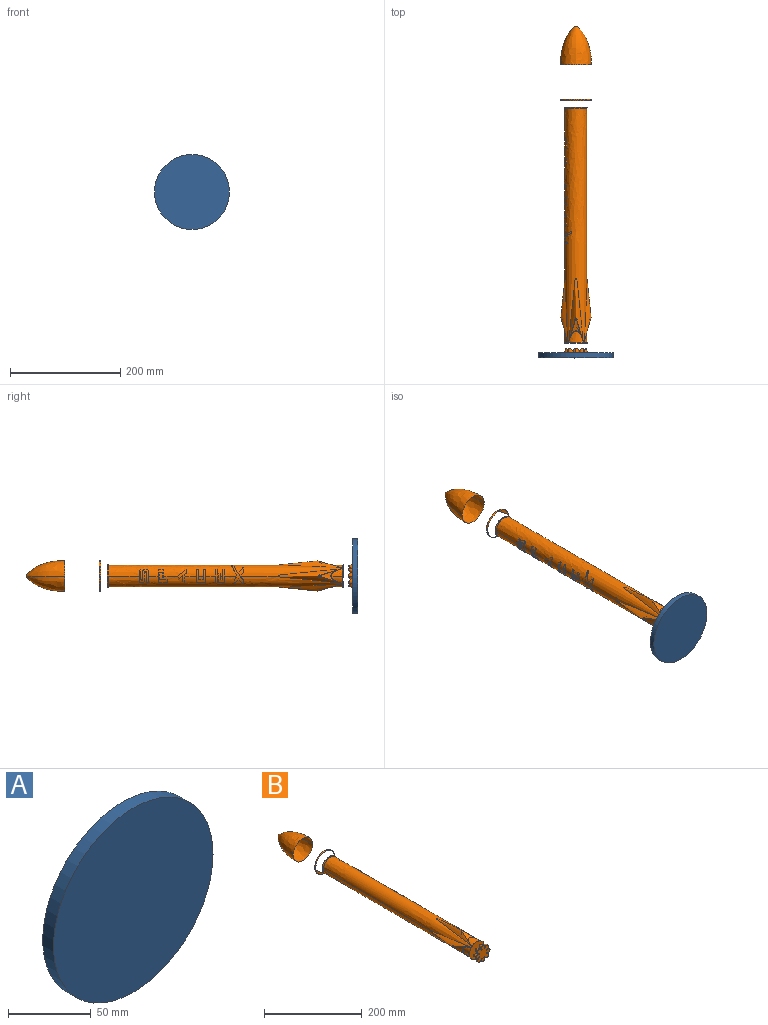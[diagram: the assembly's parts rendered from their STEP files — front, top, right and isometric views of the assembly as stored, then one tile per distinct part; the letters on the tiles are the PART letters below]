
ASSEMBLY  parts=2 mates=1
PART A: 3 faces, bbox 136.1x9.1x136.1 mm
  f0: cylinder r=68.04mm len=136.07mm, axis (0,1,0), area 3890.1mm2, adj f1,f2
  f1: plane 136.07x136.07mm, normal (0,-1,0), area 14542mm2, adj f0
  f2: plane 136.07x136.07mm, normal (0,1,0), area 14542mm2, adj f0
PART B: 144 faces, bbox 56.3x592.9x112.6 mm
  f0: revolved ~5.53x5.53mm, area 27.6mm2, adj f1,f2
  f1: bspline ~69.44x56.06mm, area 4837.5mm2, adj f0,f2,f3
  f2: bspline ~69.44x56.06mm, area 4837.5mm2, adj f0,f1,f3
  f3: revolved ~62.16x56.06mm, area 10948.1mm2, adj f1,f2,f5,f6
  f4: revolved ~13.15x4.18mm, area 53.4mm2, adj f7,f8,f9,f10,f11,f12,f13,f14
  f5: bspline ~56.26x56.26mm, area 228.4mm2, adj f3,f6,f26
  f6: bspline ~56.26x56.26mm, area 228.4mm2, adj f3,f5,f26
  f7: plane 11.52x1.77mm, normal (0,-1,0), area 11.4mm2, adj f4,f8,f14,f32
  f8: bspline ~1.42x1.31mm, area 1.8mm2, adj f4,f7,f9,f32
  f9: plane 1.9x0.94mm, normal (0.33,0,-0.94), area 1.9mm2, adj f4,f8,f10,f32
  f10: bspline ~1.42x1.31mm, area 1.8mm2, adj f4,f9,f11,f32
  f11: plane 11.52x1.77mm, normal (0,1,0), area 11.4mm2, adj f4,f10,f12,f32
  f12: bspline ~1.42x1.31mm, area 1.8mm2, adj f4,f11,f13,f32
  f13: plane 1.9x0.94mm, normal (0.33,0,0.94), area 1.9mm2, adj f4,f12,f14,f32
  f14: bspline ~1.42x1.31mm, area 1.8mm2, adj f4,f7,f13,f32
  f15: revolved ~14.89x8.99mm, area 71.2mm2, adj f42,f43,f44,f45,f46
  f16: bspline ~1.41x1.29mm, area 1.8mm2, adj f17,f36,f50,f51
  f17: plane 2.64x0.95mm, normal (0.31,0,-0.95), area 2.6mm2, adj f16,f18,f36,f51
  f18: bspline ~1.41x1.29mm, area 1.8mm2, adj f17,f36,f51,f52
  f19: bspline ~1.42x1.31mm, area 1.8mm2, adj f20,f34,f57,f58
  f20: plane 7.86x0.94mm, normal (0.34,0,-0.94), area 7.9mm2, adj f19,f21,f34,f58
  f21: bspline ~1.42x1.31mm, area 1.8mm2, adj f20,f34,f58,f59
  f22: bspline ~1.43x1.32mm, area 1.8mm2, adj f23,f31,f70,f71
  f23: plane 0.94x0.91mm, normal (0.35,0,-0.94), area 0.9mm2, adj f22,f24,f31,f71
  f24: bspline ~1.43x1.32mm, area 1.8mm2, adj f23,f31,f71,f72
  f25: plane 0.85x0.53mm, normal (-0.53,0,-0.85), area 0.1mm2, adj f31,f72,f73,f122
  f26: revolved ~54.74x54.74mm, area 2077.2mm2, adj f5,f6,f74,f79
  f27: bspline ~1.44x1.33mm, area 1.8mm2, adj f28,f31,f84,f85
  f28: plane 1.19x0.93mm, normal (0.36,0,0.93), area 1.2mm2, adj f27,f29,f31,f85
  f29: bspline ~1.44x1.33mm, area 1.8mm2, adj f28,f31,f85,f86
  f30: plane 0.81x0.59mm, normal (-0.59,0,0.81), area 0mm2, adj f31,f86,f87,f123
  f31: revolved ~24.2x16.72mm, area 269.3mm2, adj f22,f23,f24,f25,f27,f28,f29,f30
  f32: revolved ~23.53x16.67mm, area 231.4mm2, adj f7,f8,f9,f10,f11,f12,f13,f14
  f33: revolved ~23.91x17.45mm, area 145.1mm2, adj f62,f63,f96,f97,f98,f100,f101,f102
  f34: revolved ~23.7x16.74mm, area 216.4mm2, adj f19,f20,f21,f55,f56,f57,f59,f60
  f35: revolved ~22.62x3.4mm, area 70.7mm2, adj f54,f108,f109,f110
  f36: revolved ~22.62x11.34mm, area 156.1mm2, adj f16,f17,f18,f49,f50,f52,f53,f111
  f37: bspline ~26.66x19.23mm, area 37mm2, adj f38,f47,f119,f122,f123
  f38: revolved ~33.39x21.59mm, area 240.3mm2, adj f37,f47,f48,f114,f115,f116,f117,f118
  f39: bspline ~42.13x25.89mm, area 196.5mm2, adj f40,f122
  f40: bspline ~114.91x26.05mm, area 1689.4mm2, adj f39,f122
  f41: revolved ~112.99x11.46mm, area 1.2mm2, adj f120,f122
  f42: bspline ~7.58x5.38mm, area 9.3mm2, adj f15,f43,f46,f122,f123
  f43: plane 7.23x5.03mm, normal (0,-1,0), area 8mm2, adj f15,f42,f44,f122
  f44: bspline ~1.13x1.12mm, area 1.5mm2, adj f15,f43,f45,f122
  f45: bspline ~10.18x7.96mm, area 13.7mm2, adj f15,f44,f46,f122
  f46: bspline ~4.76x3.62mm, area 5.9mm2, adj f15,f42,f45,f122,f123
  f47: plane 2.36x0.92mm, normal (-0.92,0,-0.39), area 2.4mm2, adj f37,f38,f48,f122
  f48: bspline ~19.09x13.11mm, area 25.4mm2, adj f38,f47,f114,f122
  f49: plane 3.2x0.85mm, normal (-0.53,0,-0.85), area 3.2mm2, adj f36,f50,f113,f122
  f50: plane 16.59x4.13mm, normal (0,1,0), area 16.8mm2, adj f16,f36,f49,f51,f122
  f51: revolved ~6.24x4.93mm, area 30mm2, adj f16,f17,f18,f50,f52,f122
  f52: plane 9.33x1.73mm, normal (0,-1,0), area 9.2mm2, adj f18,f36,f51,f53,f122
  f53: plane 3.2x0.98mm, normal (-0.19,0,-0.98), area 3.2mm2, adj f36,f52,f111,f122
  f54: plane 2.96x0.85mm, normal (-0.53,0,-0.85), area 3mm2, adj f35,f108,f110,f122
  f55: bspline ~3.04x2.86mm, area 4.5mm2, adj f34,f56,f107,f122
  f56: plane 0.83x0.56mm, normal (-0.56,0,-0.83), area 0.5mm2, adj f34,f55,f57,f122
  f57: plane 17.59x4.42mm, normal (0,1,0), area 17.9mm2, adj f19,f34,f56,f58,f122
  f58: revolved ~10.14x6.73mm, area 68.4mm2, adj f19,f20,f21,f57,f59,f122
  f59: plane 17.59x4.42mm, normal (0,-1,0), area 17.9mm2, adj f21,f34,f58,f60,f122
  f60: plane 0.83x0.56mm, normal (-0.56,0,-0.83), area 0.3mm2, adj f34,f59,f61,f122
  f61: bspline ~3.04x2.86mm, area 4.5mm2, adj f34,f60,f103,f122
  f62: bspline ~3.64x2.9mm, area 4.6mm2, adj f33,f63,f102,f122
  f63: plane 6.56x3.76mm, normal (0,-1,0), area 6.8mm2, adj f33,f62,f96,f122
  f64: bspline ~3.03x2.86mm, area 4.5mm2, adj f32,f65,f95,f122
  f65: plane 4.52x0.83mm, normal (-0.56,0,-0.83), area 4.5mm2, adj f32,f64,f66,f122
  f66: bspline ~3.03x2.86mm, area 4.5mm2, adj f32,f65,f89,f122
  f67: bspline ~3.54x3.43mm, area 5.4mm2, adj f31,f68,f88,f122
  f68: plane 3.56x0.82mm, normal (-0.57,0,-0.82), area 3.6mm2, adj f31,f67,f69,f122
  f69: bspline ~3.54x3.43mm, area 5.4mm2, adj f31,f68,f70,f122
  f70: plane 14.91x2.86mm, normal (0,1,0), area 14.9mm2, adj f22,f31,f69,f71,f122
  f71: revolved ~6.94x3.19mm, area 21.3mm2, adj f22,f23,f24,f70,f72,f122
  f72: plane 17.3x4.1mm, normal (0,-1,0), area 17.6mm2, adj f24,f25,f31,f71,f122
  f73: bspline ~3.16x2.97mm, area 4.7mm2, adj f25,f31,f80,f122
  f74: bspline ~41.71x41.71mm, area 165.5mm2, adj f26,f79,f122
  f75: bspline ~42.13x25.89mm, area 202mm2, adj f76,f123
  f76: bspline ~114.91x26.05mm, area 1689.4mm2, adj f75,f123
  f77: bspline ~42.4x26.05mm, area 237.2mm2, adj f78,f122,f123
  f78: bspline ~114.91x26.05mm, area 1689.4mm2, adj f77,f122,f123
  f79: bspline ~41.71x41.71mm, area 165.5mm2, adj f26,f74,f123
  f80: plane 16.86x2.72mm, normal (0,1,0), area 16.9mm2, adj f31,f73,f81,f122,f123
  f81: bspline ~3.56x3.43mm, area 5.4mm2, adj f31,f80,f82,f123
  f82: plane 2.95x0.83mm, normal (-0.56,0,0.83), area 2.9mm2, adj f31,f81,f83,f123
  f83: bspline ~3.56x3.43mm, area 5.4mm2, adj f31,f82,f84,f123
  f84: plane 14.81x2.74mm, normal (0,-1,0), area 14.8mm2, adj f27,f31,f83,f85,f123
  f85: revolved ~7.1x3.47mm, area 23.9mm2, adj f27,f28,f29,f84,f86,f123
  f86: plane 18.65x4.88mm, normal (0,1,0), area 19.1mm2, adj f29,f30,f31,f85,f123
  f87: bspline ~3.52x3.43mm, area 5.4mm2, adj f30,f31,f88,f123
  f88: plane 18x3.08mm, normal (0,-1,0), area 18.2mm2, adj f31,f67,f87,f122,f123
  f89: plane 19.93x3.92mm, normal (0,1,0), area 20.3mm2, adj f32,f66,f90,f122,f123
  f90: bspline ~1.53x1.47mm, area 1.8mm2, adj f32,f89,f91,f123
  f91: plane 15.53x0.83mm, normal (-0.56,0,0.83), area 15.5mm2, adj f32,f90,f92,f123
  f92: plane 5.23x3.31mm, normal (0,-1,0), area 5.4mm2, adj f32,f91,f93,f123
  f93: plane 5.3x0.94mm, normal (0.33,0,-0.94), area 5.3mm2, adj f32,f92,f94,f123
  f94: bspline ~1.42x1.31mm, area 1.8mm2, adj f32,f93,f95,f123
  f95: plane 14.9x3.03mm, normal (0,-1,0), area 14.9mm2, adj f32,f64,f94,f122,f123
  f96: bspline ~17.45x12.79mm, area 21.9mm2, adj f33,f63,f97,f122,f123
  f97: bspline ~3.93x3.42mm, area 5.1mm2, adj f33,f96,f98,f123
  f98: bspline ~6.69x5.16mm, area 8.4mm2, adj f33,f97,f99,f100,f123
  f99: revolved ~1.12x0.83mm, area 0.5mm2, adj f98,f100,f123
  f100: plane 10.56x3.33mm, normal (0,1,0), area 10.7mm2, adj f33,f98,f99,f101,f123
  f101: bspline ~3.19x2.82mm, area 4.2mm2, adj f33,f100,f102,f123
  f102: plane 14.86x4.67mm, normal (0,-1,0), area 15.3mm2, adj f33,f62,f101,f122,f123
  f103: plane 18.53x3.19mm, normal (0,1,0), area 18.7mm2, adj f34,f61,f104,f122,f123
  f104: bspline ~3.02x2.86mm, area 4.5mm2, adj f34,f103,f105,f123
  f105: plane 11.03x0.82mm, normal (-0.58,0,0.82), area 11mm2, adj f34,f104,f106,f123
  f106: bspline ~3.02x2.86mm, area 4.5mm2, adj f34,f105,f107,f123
  f107: plane 18.53x3.19mm, normal (0,-1,0), area 18.7mm2, adj f34,f55,f106,f122,f123
  f108: plane 22.62x4.25mm, normal (0,1,0), area 23.3mm2, adj f35,f54,f109,f122,f123
  f109: plane 2.96x0.84mm, normal (-0.55,0,0.84), area 3mm2, adj f35,f108,f110,f123
  f110: plane 22.62x4.25mm, normal (0,-1,0), area 23.3mm2, adj f35,f54,f109,f122,f123
  f111: plane 15.36x4.25mm, normal (0,1,0), area 15.7mm2, adj f36,f53,f112,f122,f123
  f112: plane 11.34x0.84mm, normal (-0.55,0,0.84), area 11.3mm2, adj f36,f111,f113,f123
  f113: plane 22.62x4.25mm, normal (0,-1,0), area 23.3mm2, adj f36,f49,f112,f122,f123
  f114: bspline ~6.63x4.67mm, area 8.1mm2, adj f38,f48,f115,f122,f123
  f115: plane 7.39x4.72mm, normal (0,1,0), area 8mm2, adj f38,f114,f116,f123
  f116: bspline ~1.14x1.11mm, area 1.5mm2, adj f38,f115,f117,f123
  f117: bspline ~8.82x6.79mm, area 11.7mm2, adj f38,f116,f118,f123
  f118: bspline ~9.16x8.96mm, area 14mm2, adj f38,f117,f119,f123
  f119: plane 6.72x4.57mm, normal (0,-1,0), area 7.3mm2, adj f37,f38,f118,f123
  f120: bspline ~114.91x26.05mm, area 1689.4mm2, adj f41,f121,f122,f123
  f121: bspline ~42.13x25.89mm, area 194.4mm2, adj f120,f122,f123
  f122: revolved ~424.11x39.85mm, area 23010.7mm2, adj f25,f37,f39,f40,f41,f42,f43,f44
  f123: revolved ~424.11x39.85mm, area 22809mm2, adj f30,f37,f42,f46,f75,f76,f77,f78
  f124: revolved ~43.18x43.18mm, area 613.7mm2, adj f122,f123,f125
  f125: revolved ~43.18x43.18mm, area 635.7mm2, adj f124,f140
  f126: bspline ~9.63x8.72mm, area 66.4mm2, adj f127,f140,f142
  f127: bspline ~9.59x8.67mm, area 66.4mm2, adj f126,f140,f142
  f128: bspline ~10.23x9.45mm, area 66.4mm2, adj f129,f140,f142
  f129: bspline ~10.23x9.45mm, area 66.4mm2, adj f128,f140,f142
  f130: bspline ~9.63x8.72mm, area 66.4mm2, adj f131,f140,f142
  f131: bspline ~9.63x8.72mm, area 66.4mm2, adj f130,f140,f142
  f132: bspline ~10.23x9.45mm, area 66.4mm2, adj f133,f140,f142
  f133: bspline ~10.23x9.45mm, area 66.4mm2, adj f132,f140,f142
  f134: bspline ~9.63x8.72mm, area 66.4mm2, adj f135,f140,f142
  f135: bspline ~9.59x8.67mm, area 66.4mm2, adj f134,f140,f142
  f136: bspline ~8.87x8.67mm, area 66.4mm2, adj f137,f140,f142
  f137: bspline ~10.23x9.45mm, area 66.4mm2, adj f136,f140,f142
  f138: bspline ~9.63x8.72mm, area 66.4mm2, adj f139,f140,f142
  f139: bspline ~9.59x8.67mm, area 66.4mm2, adj f138,f140,f142
  f140: revolved ~43.18x43.18mm, area 1749.6mm2, adj f125,f126,f127,f128,f129,f130,f131,f132
  f141: bspline ~10.23x9.45mm, area 66.4mm2, adj f140,f142,f143
  f142: plane 40.38x40.38mm, normal (0,-1,0), area 1020.3mm2, adj f126,f127,f128,f129,f130,f131,f132,f133
  f143: bspline ~8.87x8.67mm, area 66.4mm2, adj f140,f141,f142
PLACE A t=(117.24,-302.51,63.64)mm fixed
PLACE B rot(axis=(0,1,0),180deg) t=(418.83,-327.67,63.64)mm
MATE fastened B.f142 <-> A.f0  axis (0,-1,0) through (117.24,-302.51,63.64)mm
